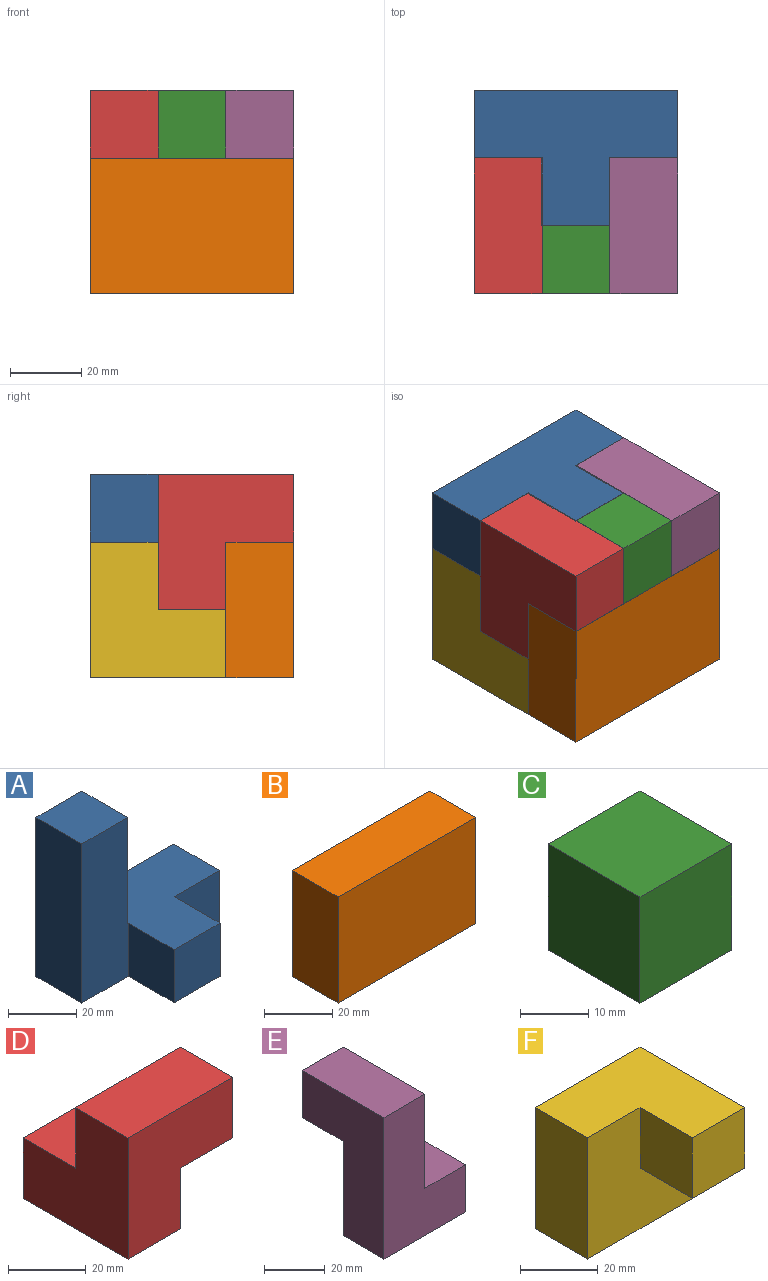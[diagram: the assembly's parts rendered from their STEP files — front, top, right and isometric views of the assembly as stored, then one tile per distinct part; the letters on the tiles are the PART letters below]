
ASSEMBLY  parts=6 mates=19
PART A: 12 faces, bbox 57.2x38.1x57.2 mm
  f0: plane 57.15x19.29mm, normal (0,-1,0), area 1093.2mm2, adj f1,f2,f3,f5,f6,f9
  f1: plane 19.05x19.05mm, normal (0,0,1), area 362.9mm2, adj f0,f2,f6,f8
  f2: plane 57.15x19.05mm, normal (-1,0,0), area 1088.7mm2, adj f0,f1,f3,f8
  f3: plane 57.15x38.1mm, normal (0,0,-1), area 1451.6mm2, adj f0,f2,f4,f7,f8,f9,f10,f11
  f4: plane 19.05x19.05mm, normal (1,0,0), area 362.9mm2, adj f3,f5,f7,f8
  f5: plane 38.1x38.1mm, normal (0,0,1), area 1088.7mm2, adj f0,f4,f6,f7,f8,f9,f10,f11
  f6: plane 38.1x19.05mm, normal (1,0,0), area 725.8mm2, adj f0,f1,f5,f8
  f7: plane 19.05x18.81mm, normal (0,-1,0), area 358.4mm2, adj f3,f4,f5,f10
  f8: plane 57.15x57.15mm, normal (0,1,0), area 1814.5mm2, adj f1,f2,f3,f4,f5,f6
  f9: plane 19.05x19.05mm, normal (-1,0,0), area 362.9mm2, adj f0,f3,f5,f11
  f10: plane 19.05x19.05mm, normal (1,0,0), area 362.9mm2, adj f3,f5,f7,f11
  f11: plane 19.05x19.05mm, normal (0,-1,0), area 362.9mm2, adj f3,f5,f9,f10
PART B: 6 faces, bbox 57.2x19.1x38.1 mm
  f0: plane 38.1x19.05mm, normal (-1,0,0), area 725.8mm2, adj f1,f3,f4,f5
  f1: plane 57.15x19.05mm, normal (0,0,-1), area 1088.7mm2, adj f0,f2,f4,f5
  f2: plane 38.1x19.05mm, normal (1,0,0), area 725.8mm2, adj f1,f3,f4,f5
  f3: plane 57.15x19.05mm, normal (0,0,1), area 1088.7mm2, adj f0,f2,f4,f5
  f4: plane 57.15x38.1mm, normal (0,-1,0), area 2177.4mm2, adj f0,f1,f2,f3
  f5: plane 57.15x38.1mm, normal (0,1,0), area 2177.4mm2, adj f0,f1,f2,f3
PART C: 6 faces, bbox 19.1x19.1x19.1 mm
  f0: plane 19.05x19.05mm, normal (0,-1,0), area 362.9mm2, adj f1,f3,f4,f5
  f1: plane 19.05x19.05mm, normal (0,0,-1), area 362.9mm2, adj f0,f2,f4,f5
  f2: plane 19.05x19.05mm, normal (0,1,0), area 362.9mm2, adj f1,f3,f4,f5
  f3: plane 19.05x19.05mm, normal (0,0,1), area 362.9mm2, adj f0,f2,f4,f5
  f4: plane 19.05x19.05mm, normal (1,0,0), area 362.9mm2, adj f0,f1,f2,f3
  f5: plane 19.05x19.05mm, normal (-1,0,0), area 362.9mm2, adj f0,f1,f2,f3
PART D: 10 faces, bbox 38.1x38.1x38.1 mm
  f0: plane 38.1x19.05mm, normal (0,1,0), area 725.8mm2, adj f1,f4,f5,f6,f8
  f1: plane 38.1x38.1mm, normal (-1,0,0), area 1088.7mm2, adj f0,f2,f6,f7,f8,f9
  f2: plane 38.1x19.05mm, normal (0,0,-1), area 725.8mm2, adj f1,f3,f7,f9
  f3: plane 38.1x19.05mm, normal (1,0,0), area 725.8mm2, adj f2,f4,f7,f8,f9
  f4: plane 19.05x19.05mm, normal (0,0,-1), area 362.9mm2, adj f0,f3,f5,f7
  f5: plane 19.05x19.05mm, normal (1,0,0), area 362.9mm2, adj f0,f4,f6,f7
  f6: plane 38.1x19.05mm, normal (0,0,1), area 725.8mm2, adj f0,f1,f5,f7
  f7: plane 38.1x38.1mm, normal (0,-1,0), area 1088.7mm2, adj f1,f2,f3,f4,f5,f6
  f8: plane 19.05x19.05mm, normal (0,0,1), area 362.9mm2, adj f0,f1,f3,f9
  f9: plane 19.05x19.05mm, normal (0,1,0), area 362.9mm2, adj f1,f2,f3,f8
PART E: 10 faces, bbox 38.1x38.1x57.2 mm
  f0: plane 38.1x38.1mm, normal (0,1,0), area 1088.7mm2, adj f2,f3,f4,f5,f6,f8
  f1: plane 38.1x19.05mm, normal (0,0,1), area 725.8mm2, adj f2,f6,f7,f9
  f2: plane 57.15x38.1mm, normal (-1,0,0), area 1451.6mm2, adj f0,f1,f3,f7,f8,f9
  f3: plane 38.1x19.05mm, normal (0,0,-1), area 725.8mm2, adj f0,f2,f4,f7
  f4: plane 19.05x19.05mm, normal (1,0,0), area 362.9mm2, adj f0,f3,f5,f7
  f5: plane 19.05x19.05mm, normal (0,0,1), area 362.9mm2, adj f0,f4,f6,f7
  f6: plane 38.1x38.1mm, normal (1,0,0), area 1088.7mm2, adj f0,f1,f5,f7,f8,f9
  f7: plane 57.15x38.1mm, normal (0,-1,0), area 1451.6mm2, adj f1,f2,f3,f4,f5,f6
  f8: plane 19.05x19.05mm, normal (0,0,-1), area 362.9mm2, adj f0,f2,f6,f9
  f9: plane 19.05x19.05mm, normal (0,1,0), area 362.9mm2, adj f1,f2,f6,f8
PART F: 9 faces, bbox 38.1x38.1x38.1 mm
  f0: plane 38.1x19.05mm, normal (-1,0,0), area 725.8mm2, adj f1,f3,f4,f5
  f1: plane 38.1x19.05mm, normal (0,0,-1), area 725.8mm2, adj f0,f2,f4,f5
  f2: plane 38.1x38.1mm, normal (1,0,0), area 1088.7mm2, adj f1,f3,f4,f5,f7,f8
  f3: plane 38.1x38.1mm, normal (0,0,1), area 1088.7mm2, adj f0,f2,f4,f5,f6,f8
  f4: plane 38.1x38.1mm, normal (0,-1,0), area 1088.7mm2, adj f0,f1,f2,f3,f6,f7
  f5: plane 38.1x38.1mm, normal (0,1,0), area 1451.6mm2, adj f0,f1,f2,f3
  f6: plane 19.05x19.05mm, normal (-1,0,0), area 362.9mm2, adj f3,f4,f7,f8
  f7: plane 19.05x19.05mm, normal (0,0,-1), area 362.9mm2, adj f2,f4,f6,f8
  f8: plane 19.05x19.05mm, normal (0,-1,0), area 362.9mm2, adj f2,f3,f6,f7
PLACE A rot(axis=(0,1,0),180deg) t=(61.84,-25.49,-64.52)mm
PLACE B t=(4.69,-63.59,-121.67)mm
PLACE C rot(axis=(0,0,-1),90deg) t=(23.74,-44.54,-83.57)mm
PLACE D rot(axis=(0,0,-1),90deg) t=(23.74,-44.54,-102.62)mm
PLACE E rot(axis=(-0.71,0.71,0),180deg) t=(42.79,-44.54,-64.52)mm
PLACE F rot(axis=(0,1,0),180deg) t=(42.79,-25.49,-83.57)mm
MATE planar B.f3 <-> C.f1  axis (0,0,1) through (33.27,-73.12,-83.57)mm
MATE planar C.f4 <-> D.f5  axis (0,-1,0) through (33.27,-82.64,-74.04)mm
MATE planar D.f1 <-> A.f7  axis (0,1,0) through (20.57,-44.54,-86.74)mm
MATE planar D.f2 <-> F.f7  axis (0,0,-1) through (23.74,-54.07,-102.62)mm
MATE planar B.f4 <-> D.f5  axis (0,-1,0) through (33.27,-82.64,-102.62)mm
MATE planar F.f0 <-> A.f6  axis (1,0,0) through (42.79,-35.02,-102.62)mm
MATE planar A.f6 <-> F.f0  axis (-1,0,0) through (42.79,-35.02,-102.62)mm
MATE planar E.f1 <-> F.f3  axis (0,0,-1) through (42.79,-54.07,-121.67)mm
MATE planar F.f1 <-> A.f5  axis (0,0,1) through (23.74,-35.02,-83.57)mm
MATE planar A.f1 <-> F.f3  axis (0,0,-1) through (52.32,-35.02,-121.67)mm
MATE planar A.f2 <-> E.f7  axis (1,0,0) through (61.84,-35.02,-93.09)mm
MATE planar B.f0 <-> D.f7  axis (-1,0,0) through (4.69,-73.12,-102.62)mm
MATE planar C.f0 <-> D.f0  axis (-1,0,0) through (23.74,-73.12,-74.04)mm
MATE planar E.f2 <-> F.f4  axis (0,1,0) through (47.55,-44.54,-97.86)mm
MATE planar C.f3 <-> D.f6  axis (0,0,1) through (33.27,-73.12,-64.52)mm
MATE planar D.f7 <-> A.f4  axis (-1,0,0) through (4.69,-60.42,-80.39)mm
MATE planar A.f0 <-> F.f4  axis (0,-1,0) through (52.28,-44.54,-93.01)mm
MATE planar E.f9 <-> F.f6  axis (-1,0,0) through (23.74,-54.07,-112.14)mm
MATE planar D.f9 <-> E.f0  axis (1,0,0) through (42.79,-54.07,-93.09)mm
